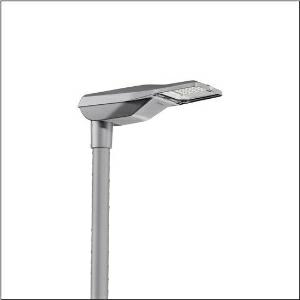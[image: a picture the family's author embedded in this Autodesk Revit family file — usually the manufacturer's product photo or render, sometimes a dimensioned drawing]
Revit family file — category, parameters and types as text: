
# Revit family: streetlight_sl_21_iq_micro___st1_5a_5xe1p31g08db_6e7e
name_source: partatom
category: Lighting Fixtures
units: mm (PartAtom-declared; Revit-internal decimal feet)

## family parameters
Cut with Voids When Loaded = No
Host = Face
Light Source = No
Part Type = Normal
Room Calculation Point = No
Round Connector Dimension = Use Diameter
Shared = No

## types (1)
- --- (1 x LED, 4730 lm, 36.4 W, 3000K)
    Apparent Load = 36 VA
    CIE Flux Codes = 22 53 95 100 100
    Color Rendering = 70
    Color Temperature = 3000K
    Default Elevation = 1800 mm
    Description = Streetlight SL 21 iQ micro, mast luminaire, primary light control with lens, of PMMA, primary optical cover: cover, of toughened safety glass, transparent, light distribution: ST1.5a, light emission: direct distribution, primary light characteristic: asymmetric, installation type: post-top, side-entry, LED, High Power LED, rated luminous flux: 4.730lm, luminous efficacy: 130lm/W, light colour: 730, colour temperature: 3000K, control gear: iQ Street-Remote, control: Street-Remote, Auto-Match, Temp-Guard, Lumen-Switch, Night-Set, Smart-Wire, Light-Fading, Desk-Remote (wireless, voltage-free reading and setting of iQ features in the workshop via application-optimized NFC function/RFID function), optimised constant luminous flux control (CLO 2.0), pre-setting: linear dimming characteristic, mains connection: 220..240V, AC, 50/60Hz, start of lifetime: 36W, end of service life: 38W, reduction: 16W, luminaire housing, of diecast aluminium, powder-coated, Siteco® metallic grey (DB 702S), corrosivity category C5 mid according to DIN EN ISO 12944, please order mast flange separately, inclination adjustable: 0°, 5°, 10°, 15°, sealing non-destructively replaceable, multi-level sealing system, length: 528mm, width: 235mm, height: 110mm, mast flange for spigot size: 42mm (side-entry): 5XC10008XM4, 60/48mm (side-entry/post-top): 5XC10108XM2, 76/60mm (side-entry/post-top): 5XC10108XM1, protection rating (complete): IP66, insulation class (complete): insulation class II (safety insulation), certification: CE, ENEC, ENEC+, VDE, impact resistance: IK10, permissible operating ambient temperature for outdoor applications: -40..+50°C, standard-compliant lighting for roads and squares, packaging unit: 1 piece

Light Distribution: ST1.5a
    Height = 110 mm
    Lamp = 1 x LED
    Lamp Light Flux = 4730 lm
    Lamp Power = 36.4 W
    Lamp count = 1
    Length = 528 mm
    Luminous efficacy = 130 lm/W
    Manufacturer = Siteco
    ModVariant = No
    Model = 5XE1P31G08DB
    Number of Poles = 1
    OnlyDefault = Yes
    Power Factor = 1
    Product Name = Streetlight SL 21 iQ micro | ST1.5a
    Product group = mast luminaire | pylon top
    ProductGroupID = 6100
    Protection Class = Protection class II
    Protection Degree = IP 66
    RLX_Detail_Level = 1
    RLX_Emergency_Light_Flux = 0 lm
    RLX_Emergency_Type = 0
    RLX_Emergency_Type_DB = No
    RlxData = <blob elided: 102797 chars, md5=7d49c7fe>
    Socket = socket
    Standby Power = 0 W
    System Light Flux = 4730 lm
    System Power = 36 W
    Type Comments = factory setting: luminous flux: 100 % | dim-lin: 254 | 715 mA
    Type Image = l_1006881.jpg
    URL = http://relux.com
    VarID = @adj_175343
    Voltage = 0 V
    Weight = 0.00 kg
    Width = 235 mm

## geometry (parser evidence)
native form markers: Blend x4, Sweep x12
no freeform markers — native parametric forms only
